# Revit family: Haworth_Pergola_Ceiling_LightTrough
name_source: partatom
category: Furniture Systems
revit_build: Autodesk Revit 2018 (Build: 20170223_1515(x64)
units: mm (PartAtom-declared; Revit-internal decimal feet)

## family parameters
Always vertical = Yes
Cut with Voids When Loaded = No
OmniClass Number = 23.40.70.14.64.21
OmniClass Title = Systems Furniture
Part Type = Normal
Room Calculation Point = No
Round Connector Dimension = Use Diameter
Shared = No
Work Plane-Based = No

## types (7) — shared parameters
Actual Depth = 5.331 "
Actual Height = 2.623 "
Assembly Code = E2020200
Description = Haworth - Pergola Light Trough
Manufacturer = Haworth
Max. Width = 144 "
Min. Width = 46 "
Model = Haworth Pergola
Revision Number = 1
Size = Verify Final Dim. w/ Haworth
Standard Width = 46, 48, 70, 72, 96, 120, 144 in.
Sustainability Info = http://www.haworth.com
Trim Finish = Haworth _ Paint _ Undecided _ Pergola
URL = http://www.haworth.com
URL - Product = https://www.haworth.com
Warranty = http://www.haworth.com

## per-type parameters (varying)
| type | Actual Width | Width |
| 48w | 48 " | 48 " |
| 46w | 46 " | 46 " |
| 70w | 70 " | 70 " |
| 72w | 72 " | 72 " |
| 96w | 96 " | 96 " |
| 120w | 120 " | 120 " |
| 144w | 144 " | 144 " |

## geometry (parser evidence)
native form markers: Sweep x11
no freeform markers — native parametric forms only
